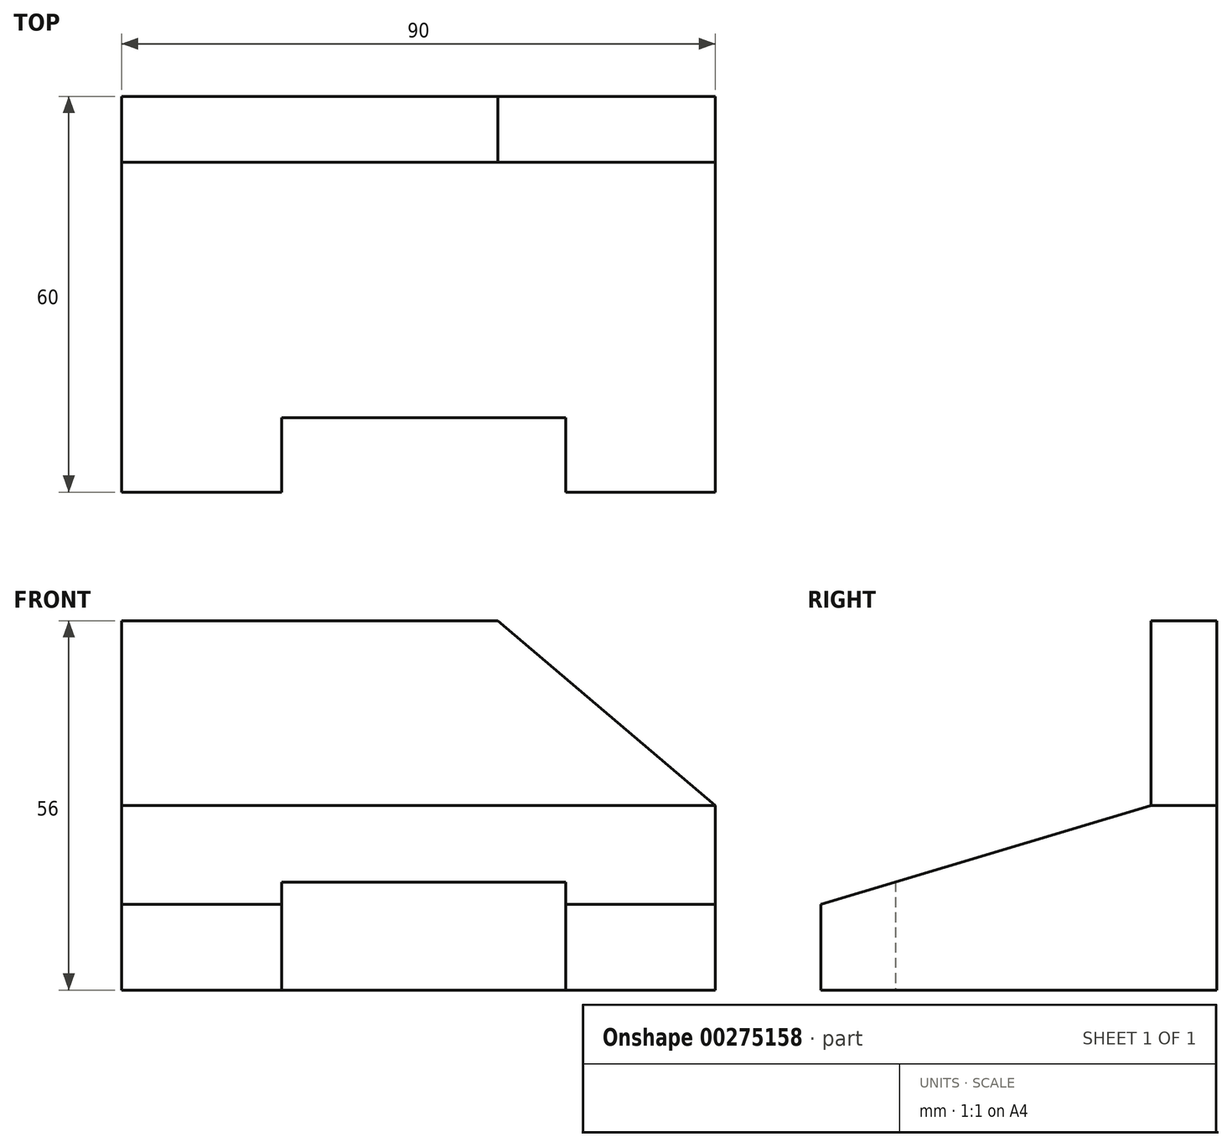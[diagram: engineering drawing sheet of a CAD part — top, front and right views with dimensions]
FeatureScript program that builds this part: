
annotation { "Feature Type Name" : "Feature", "Feature Type Description" : "" }
export const myFeature = defineFeature(function(context is Context, id is Id, definition is map)
    precondition{}
    {
        {
            var Q0;
            Q0=qCreatedBy(makeId("Right.planeOp"),FACE);
            var sketch = newSketch(context, id + "F0", { "sketchPlane" : qUnion([Q0])});
            skLineSegment(sketch, "E0", {"start": v(-10, 56) * mm, "end": v(0, 56) * mm});
            skLineSegment(sketch, "E1", {"start": v(0, 56) * mm, "end": v(0, 0) * mm});
            skLineSegment(sketch, "E2", {"start": v(0, 0) * mm, "end": v(-60, 0) * mm});
            skLineSegment(sketch, "E3", {"start": v(-60, 0) * mm, "end": v(-60, 13) * mm});
            skLineSegment(sketch, "E4", {"start": v(-60, 13) * mm, "end": v(-10, 28) * mm});
            skLineSegment(sketch, "E5", {"start": v(-10, 28) * mm, "end": v(-10, 56) * mm});
            skSolve(sketch);
        }
        {
            var Q0;
            Q0=makeQuery(id+"F0.imprint","IMPRINT",FACE,{"disambiguationData":[TD([[makeQuery(id+"F0.imprint","IMPRINT",EDGE,{"derivedFrom":sQuery(id+"F0.wireOp",EDGE,"E0")}),-1.0]])]});
            extrude(context, id + "F1", {"entities" : qUnion([Q0]), "depth" : 90 * mm});
        }
        {
            var Q0;
            Q0=makeQuery(id+"F1.opExtrude","SWEPT_FACE",FACE,{"disambiguationData":[OSD([sQuery(id+"F0.wireOp",EDGE,"E5")])]});
            var sketch = newSketch(context, id + "F2", { "sketchPlane" : qUnion([Q0])});
            skLineSegment(sketch, "E6", {"start": v(57, 56) * mm, "end": v(90, 28) * mm});
            skSolve(sketch);
        }
        {
            var Q0;
            {var subQ0=sQuery(id+"F2.wireOp",EDGE,"E6");Q0=makeQuery(id+"F2.imprint","IMPRINT",FACE,{"disambiguationData":[TD([[makeQuery(id+"F2.imprint","IMPRINT",EDGE,{"derivedFrom":subQ0}),1.0]])]});}
            extrude(context, id + "F3", {"entities" : qUnion([Q0]), "operationType" : NewBodyOperationType.REMOVE, "oppositeDirection" : true, "depth" : 25 * mm});
        }
        {
            var Q0;
            Q0=makeQuery(id+"F1.opExtrude","SWEPT_FACE",FACE,{"disambiguationData":[OSD([sQuery(id+"F0.wireOp",EDGE,"E2")])]});
            var sketch = newSketch(context, id + "F4", { "sketchPlane" : qUnion([Q0])});
            skLineSegment(sketch, "E7.bottom", {"start": v(24.23, 48.75) * mm, "end": v(67.3, 48.75) * mm});
            skLineSegment(sketch, "E7.top", {"start": v(24.23, 60) * mm, "end": v(67.3, 60) * mm});
            skLineSegment(sketch, "E7.left", {"start": v(24.23, 48.75) * mm, "end": v(24.23, 60) * mm});
            skLineSegment(sketch, "E7.right", {"start": v(67.3, 48.75) * mm, "end": v(67.3, 60) * mm});
            skSolve(sketch);
        }
        {
            var Q0;
            Q0 = qSketchRegion(id + "F4", true);
            extrude(context, id + "F5", {"entities" : qUnion([Q0]), "operationType" : NewBodyOperationType.REMOVE, "oppositeDirection" : true, "depth" : 55 * mm});
        }
    });
